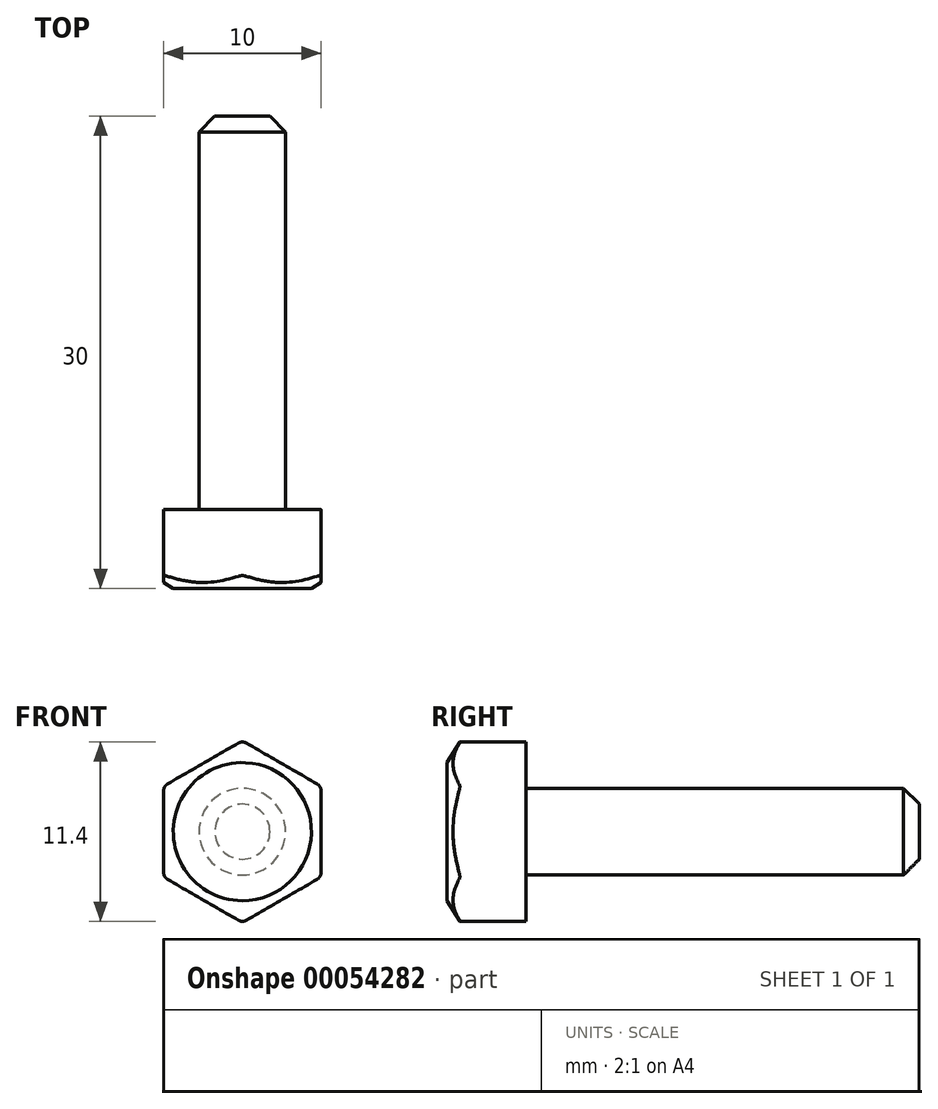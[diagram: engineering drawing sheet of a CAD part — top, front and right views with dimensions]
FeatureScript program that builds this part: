
annotation { "Feature Type Name" : "Feature", "Feature Type Description" : "" }
export const myFeature = defineFeature(function(context is Context, id is Id, definition is map)
    precondition{}
    {
        {
            var Q0;
            Q0=qCreatedBy(makeId("Front.planeOp"),FACE);
            var sketch = newSketch(context, id + "F0", { "sketchPlane" : qUnion([Q0])});
            skCircle(sketch, "E0", {"center": v(0, 0) * mm, "radius": 2.75 * mm});
            skSolve(sketch);
        }
        {
            var Q0;
            Q0=makeQuery(id+"F0.imprint","IMPRINT",FACE,{"disambiguationData":[TD([[makeQuery(id+"F0.imprint","IMPRINT",EDGE,{"derivedFrom":sQuery(id+"F0.wireOp",EDGE,"E0")}),1.0]])]});
            extrude(context, id + "F1", {"entities" : qUnion([Q0]), "oppositeDirection" : true, "depth" : 25 * mm});
        }
        {
            var Q0;
            Q0=makeQuery(id+"F1.opExtrude","CAP_EDGE",EDGE,{"disambiguationData":[OSD([sQuery(id+"F0.wireOp",EDGE,"E0")])],"isStart":false});
            chamfer(context, id + "F2", {"entities" : qUnion([Q0]), "width" : 1 * mm, "tangentPropagation" : true});
        }
        {
            var Q0;
            Q0=makeQuery(id+"F1.opExtrude","CAP_FACE",FACE,{"disambiguationData":[OSD([sQuery(id+"F0.wireOp",EDGE,"E0")])],"isStart":true});
            var sketch = newSketch(context, id + "F3", { "sketchPlane" : qUnion([Q0])});
            skCircle(sketch, "E1.cCircle", {"center": v(0, 0) * mm, "radius": 5 * mm, "construction": true});
            skLineSegment(sketch, "E1.0", {"start": v(5, 2.89) * mm, "end": v(5, -2.89) * mm});
            skLineSegment(sketch, "E1.1", {"start": v(5, -2.89) * mm, "end": v(0, -5.77) * mm});
            skLineSegment(sketch, "E1.2", {"start": v(0, -5.77) * mm, "end": v(-5, -2.89) * mm});
            skLineSegment(sketch, "E1.3", {"start": v(-5, -2.89) * mm, "end": v(-5, 2.89) * mm});
            skLineSegment(sketch, "E1.4", {"start": v(-5, 2.89) * mm, "end": v(0, 5.77) * mm});
            skLineSegment(sketch, "E1.5", {"start": v(0, 5.77) * mm, "end": v(5, 2.89) * mm});
            skPoint(sketch, "E1.0.midPoint", {"position": v(5, 0) * mm});
            skSolve(sketch);
        }
        {
            var Q0;
            Q0 = qSketchRegion(id + "F3", true);
            extrude(context, id + "F4", {"entities" : qUnion([Q0]), "operationType" : NewBodyOperationType.ADD, "depth" : 5 * mm});
        }
        {
            var Q0;
            Q0=makeQuery(id+"F4.opExtrude","SWEPT_EDGE",EDGE,{"disambiguationData":[OSD([sQuery(id+"F3.wireOp",EDGE,"E1.0"),sQuery(id+"F3.wireOp",EDGE,"E1.5")])]});
            var Q1;
            Q1=makeQuery(id+"F4.opExtrude","SWEPT_EDGE",EDGE,{"disambiguationData":[OSD([sQuery(id+"F3.wireOp",EDGE,"E1.4"),sQuery(id+"F3.wireOp",EDGE,"E1.5")])]});
            var Q2;
            Q2=makeQuery(id+"F4.opExtrude","SWEPT_EDGE",EDGE,{"disambiguationData":[OSD([sQuery(id+"F3.wireOp",EDGE,"E1.3"),sQuery(id+"F3.wireOp",EDGE,"E1.4")])]});
            var Q3;
            Q3=makeQuery(id+"F4.opExtrude","SWEPT_EDGE",EDGE,{"disambiguationData":[OSD([sQuery(id+"F3.wireOp",EDGE,"E1.1"),sQuery(id+"F3.wireOp",EDGE,"E1.2")])]});
            var Q4;
            Q4=makeQuery(id+"F4.opExtrude","SWEPT_EDGE",EDGE,{"disambiguationData":[OSD([sQuery(id+"F3.wireOp",EDGE,"E1.2"),sQuery(id+"F3.wireOp",EDGE,"E1.3")])]});
            var Q5;
            Q5=makeQuery(id+"F4.opExtrude","SWEPT_EDGE",EDGE,{"disambiguationData":[OSD([sQuery(id+"F3.wireOp",EDGE,"E1.0"),sQuery(id+"F3.wireOp",EDGE,"E1.1")])]});
            fillet(context, id + "F5", {"entities" : qUnion([Q0, Q1, Q2, Q3, Q4, Q5]), "radius" : .5 * mm, "tangentPropagation" : true, "allowEdgeOverflow" : false});
        }
        {
            var Q0;
            Q0=qCreatedBy(makeId("Right.planeOp"),FACE);
            var sketch = newSketch(context, id + "F6", { "sketchPlane" : qUnion([Q0])});
            skLineSegment(sketch, "E2", {"start": v(-5.36, 3.8) * mm, "end": v(-4, 6) * mm});
            skLineSegment(sketch, "E3", {"start": v(-4, 6) * mm, "end": v(-5.36, 6) * mm});
            skLineSegment(sketch, "E4", {"start": v(-5.36, 6) * mm, "end": v(-5.36, 3.8) * mm});
            skLineSegment(sketch, "E5", {"start": v(-9.74, 0) * mm, "end": v(0, 0) * mm});
            skSolve(sketch);
        }
        {
            var Q0;
            Q0=makeQuery(id+"F6.imprint","IMPRINT",FACE,{"disambiguationData":[TD([[makeQuery(id+"F6.imprint","IMPRINT",EDGE,{"derivedFrom":sQuery(id+"F6.wireOp",EDGE,"E2")}),1.0]])]});
            var Q1;
            Q1=sQuery(id+"F6.wireOp",EDGE,"E5");
            revolve(context, id + "F7", {"operationType" : NewBodyOperationType.REMOVE, "entities" : qUnion([Q0]), "axis" : qUnion([Q1]), "revolveType" : RevolveType.FULL, "oppositeDirection" : true});
        }
    });
